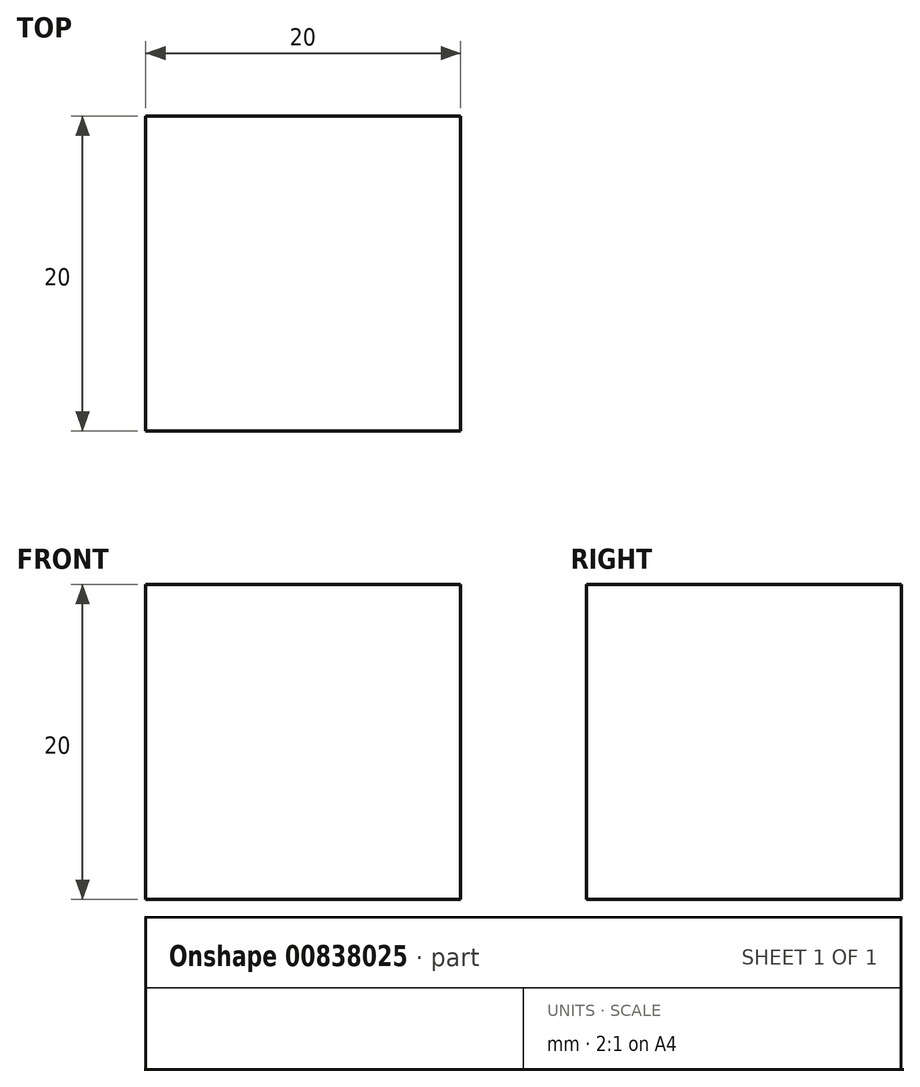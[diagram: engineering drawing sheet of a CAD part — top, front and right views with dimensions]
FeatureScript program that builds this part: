
annotation { "Feature Type Name" : "Feature", "Feature Type Description" : "" }
export const myFeature = defineFeature(function(context is Context, id is Id, definition is map)
    precondition{}
    {
        {
            var Q0;
            Q0=qCreatedBy(makeId("Top.planeOp"),FACE);
            var sketch = newSketch(context, id + "F0", { "sketchPlane" : qUnion([Q0])});
            skLineSegment(sketch, "E0.bottom", {"start": v(-13.65, 10.97) * mm, "end": v(6.35, 10.97) * mm});
            skLineSegment(sketch, "E0.top", {"start": v(-13.65, -9.03) * mm, "end": v(6.35, -9.03) * mm});
            skLineSegment(sketch, "E0.left", {"start": v(-13.65, 10.97) * mm, "end": v(-13.65, -9.03) * mm});
            skLineSegment(sketch, "E0.right", {"start": v(6.35, 10.97) * mm, "end": v(6.35, -9.03) * mm});
            skSolve(sketch);
        }
        {
            var Q0;
            Q0=makeQuery(id+"F0.imprint","IMPRINT",FACE,{"disambiguationData":[TD([[makeQuery(id+"F0.imprint","IMPRINT",EDGE,{"derivedFrom":sQuery(id+"F0.wireOp",EDGE,"E0.bottom")}),-1.0]])]});
            extrude(context, id + "F1", {"entities" : qUnion([Q0]), "depth" : 20 * mm, "offsetDistance" : 25 * mm});
        }
    });
